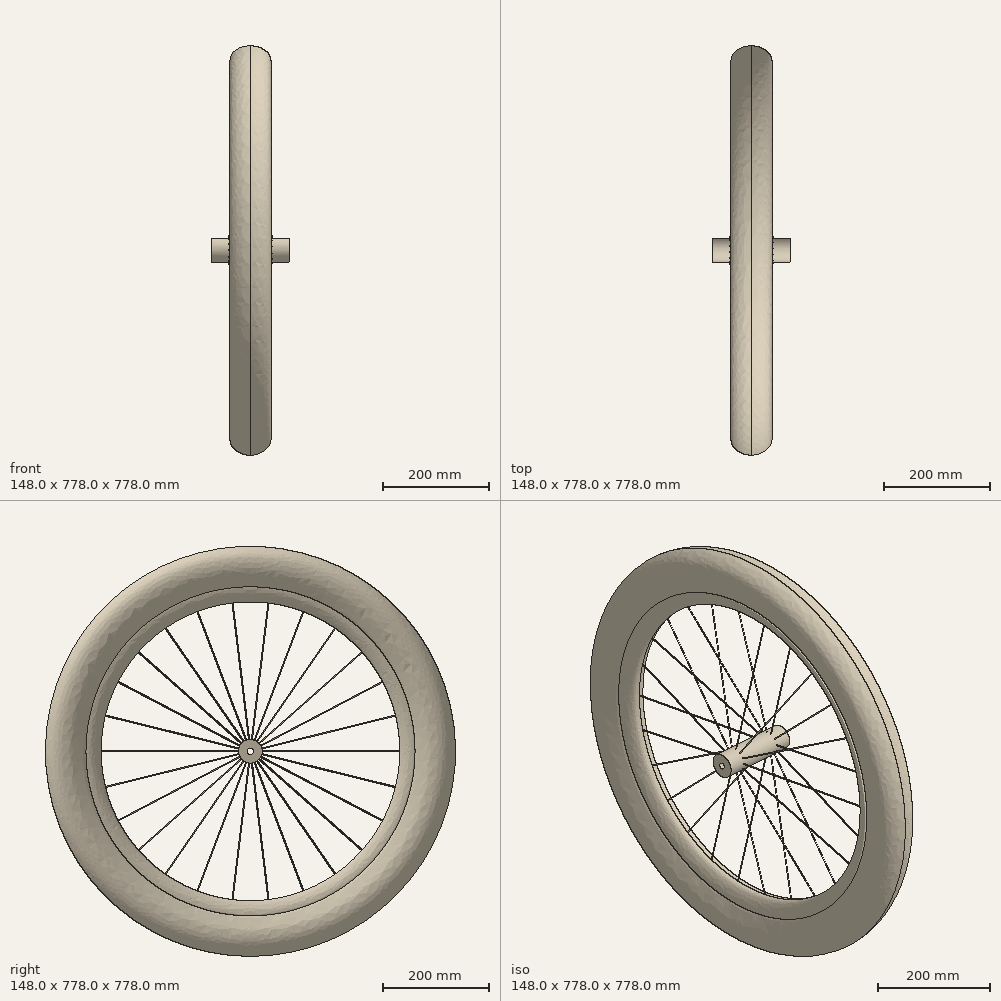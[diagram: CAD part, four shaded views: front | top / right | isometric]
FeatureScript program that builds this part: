
annotation { "Feature Type Name" : "Feature", "Feature Type Description" : "" }
export const myFeature = defineFeature(function(context is Context, id is Id, definition is map)
    precondition{}
    {
        {
            var Q0;
            Q0=qCreatedBy(makeId("Right.planeOp"),FACE);
            var sketch = newSketch(context, id + "F0", { "sketchPlane" : qUnion([Q0])});
            skCircle(sketch, "E0", {"center": v(0, 0) * mm, "radius": 311 * mm});
            skSolve(sketch);
        }
        {
            var Q0;
            Q0=qCreatedBy(makeId("Top.planeOp"),FACE);
            var sketch = newSketch(context, id + "F1", { "sketchPlane" : qUnion([Q0])});
            skFitSpline(sketch, "E1", {"points": [v(20.55, 311.57) * mm, v(21.9, 312.08) * mm, v(23.8, 311.8) * mm, v(24.17, 310.8) * mm, v(23.97, 308.06) * mm, v(22.43, 300.9) * mm, v(12.28, 286.77) * mm, v(0, 283.3) * mm], "startDerivative": vector(8.17, 18.36) * mm, "endDerivative": vector(-81.97, -0.82) * mm});
            skFitSpline(sketch, "E2", {"points": [v(20.55, 311.57) * mm, v(21.24, 310.48) * mm, v(21.34, 310.93) * mm, v(22.97, 310.97) * mm, v(23.15, 310.53) * mm, v(22.53, 305.14) * mm, v(14, 300.56) * mm, v(0, 299.7) * mm], "startDerivative": vector(-17.07, -43.86) * mm, "endDerivative": vector(-49.6, 0.02) * mm});
            skFitSpline(sketch, "E3.MirrorCS", {"points": [v(-20.55, 311.57) * mm, v(-21.9, 312.08) * mm, v(-23.8, 311.8) * mm, v(-24.17, 310.8) * mm, v(-23.97, 308.06) * mm, v(-22.43, 300.9) * mm, v(-12.28, 286.77) * mm, v(0, 283.3) * mm], "startDerivative": vector(-8.17, 18.36) * mm, "endDerivative": vector(81.97, -0.82) * mm});
            skFitSpline(sketch, "E4.MirrorCS", {"points": [v(-20.55, 311.57) * mm, v(-21.24, 310.48) * mm, v(-21.34, 310.93) * mm, v(-22.97, 310.97) * mm, v(-23.15, 310.53) * mm, v(-22.53, 305.14) * mm, v(-14, 300.56) * mm, v(0, 299.7) * mm], "startDerivative": vector(17.07, -43.86) * mm, "endDerivative": vector(49.6, 0.02) * mm});
            skSolve(sketch);
        }
        {
            var Q0;
            Q0=qCreatedBy(makeId("Top.planeOp"),FACE);
            var sketch = newSketch(context, id + "F2", { "sketchPlane" : qUnion([Q0])});
            skFitSpline(sketch, "E5", {"points": [v(22.15, 310.9) * mm, v(21.57, 310.84) * mm, v(21.34, 310.38) * mm, v(20.54, 310.2) * mm, v(20.06, 311.12) * mm, v(20.82, 312.82) * mm, v(24.67, 317.46) * mm, v(31.25, 328.9) * mm, v(37.5, 340.7) * mm, v(38.08, 364.92) * mm, v(25.3, 381.14) * mm, v(0, 389) * mm], "startDerivative": vector(-24.19, 2.88) * mm, "endDerivative": vector(-137.92, 0.5) * mm});
            skFitSpline(sketch, "E6", {"points": [v(22.15, 310.9) * mm, v(22.52, 310.86) * mm, v(22.95, 310.74) * mm, v(23.02, 309.82) * mm, v(22.71, 308.86) * mm, v(21.55, 307.96) * mm, v(19.8, 308.82) * mm, v(19.03, 310.72) * mm, v(20.54, 314.45) * mm, v(26.42, 323.36) * mm, v(32.51, 336.03) * mm, v(36, 347.14) * mm, v(34.97, 365.95) * mm, v(19.79, 381.48) * mm, v(0, 386.48) * mm], "startDerivative": vector(16.59, -2.55) * mm, "endDerivative": vector(-154.7, -0.05) * mm});
            skFitSpline(sketch, "E7.MirrorCS", {"points": [v(-22.15, 310.9) * mm, v(-22.52, 310.86) * mm, v(-22.95, 310.74) * mm, v(-23.02, 309.82) * mm, v(-22.71, 308.86) * mm, v(-21.55, 307.96) * mm, v(-19.8, 308.82) * mm, v(-19.03, 310.72) * mm, v(-20.54, 314.45) * mm, v(-26.42, 323.36) * mm, v(-32.51, 336.03) * mm, v(-36, 347.14) * mm, v(-34.97, 365.95) * mm, v(-19.79, 381.48) * mm, v(0, 386.48) * mm], "startDerivative": vector(-16.59, -2.55) * mm, "endDerivative": vector(154.7, -0.05) * mm});
            skFitSpline(sketch, "E8.MirrorCS", {"points": [v(-22.15, 310.9) * mm, v(-21.57, 310.84) * mm, v(-21.34, 310.38) * mm, v(-20.54, 310.2) * mm, v(-20.06, 311.12) * mm, v(-20.82, 312.82) * mm, v(-24.67, 317.46) * mm, v(-31.25, 328.9) * mm, v(-37.5, 340.7) * mm, v(-38.08, 364.92) * mm, v(-25.3, 381.14) * mm, v(0, 389) * mm], "startDerivative": vector(24.19, 2.88) * mm, "endDerivative": vector(137.92, 0.5) * mm});
            skSolve(sketch);
        }
        {
            var Q0;
            Q0=makeQuery(id+"F1.imprint","IMPRINT",FACE,{"disambiguationData":[TD([[makeQuery(id+"F1.imprint","IMPRINT",EDGE,{"derivedFrom":sQuery(id+"F1.wireOp",EDGE,"E1")}),-1.0]])]});
            var Q1;
            Q1=sQuery(id+"F0.wireOp",EDGE,"E0");
            revolve(context, id + "F3", {"surfaceOperationType" : NewSurfaceOperationType.NEW, "entities" : qUnion([Q0]), "axis" : qUnion([Q1]), "revolveType" : RevolveType.FULL});
        }
        {
            var Q0;
            Q0=makeQuery(id+"F2.imprint","IMPRINT",FACE,{"disambiguationData":[TD([[makeQuery(id+"F2.imprint","IMPRINT",EDGE,{"derivedFrom":sQuery(id+"F2.wireOp",EDGE,"E5")}),1.0]])]});
            var Q1;
            Q1=makeQuery(id+"F3.opRevolve","SWEPT_EDGE",EDGE,{"disambiguationData":[OSD([sQuery(id+"F1.wireOp",EDGE,"E2"),sQuery(id+"F1.wireOp",EDGE,"E4.MirrorCS")])]});
            revolve(context, id + "F4", {"operationType" : NewBodyOperationType.ADD, "surfaceOperationType" : NewSurfaceOperationType.NEW, "entities" : qUnion([Q0]), "axis" : qUnion([Q1]), "revolveType" : RevolveType.FULL});
        }
        {
            var Q0;
            Q0=qCreatedBy(makeId("Right.planeOp"),FACE);
            var sketch = newSketch(context, id + "F5", { "sketchPlane" : qUnion([Q0])});
            skCircle(sketch, "E9", {"center": v(0, 0) * mm, "radius": 6 * mm});
            skCircle(sketch, "E10", {"center": v(0, 0) * mm, "radius": 22.5 * mm});
            skSolve(sketch);
        }
        {
            var Q0;
            Q0=makeQuery(id+"F5.imprint","IMPRINT",FACE,{"disambiguationData":[TD([[makeQuery(id+"F5.imprint","IMPRINT",EDGE,{"derivedFrom":sQuery(id+"F5.wireOp",EDGE,"E9")}),-1.0]])]});
            extrude(context, id + "F6", {"entities" : qUnion([Q0]), "operationType" : NewBodyOperationType.ADD, "depth" : 148 * mm, "offsetDistance" : 25 * mm, "symmetric" : true});
        }
        {
            var Q0;
            Q0=qCreatedBy(makeId("Top.planeOp"),FACE);
            var sketch = newSketch(context, id + "F7", { "sketchPlane" : qUnion([Q0])});
            skLineSegment(sketch, "E11.MirrorCS", {"start": v(0, 283.6) * mm, "end": v(41.7, 20.08) * mm});
            skLineSegment(sketch, "E12.MirrorCS", {"start": v(0, -283.6) * mm, "end": v(-41.7, -20.08) * mm});
            skSolve(sketch);
        }
        {
            var Q0;
            Q0=sQuery(id+"F7.wireOp",EDGE,"E11.MirrorCS");
            var Q1;
            Q1=sQuery(id+"F7.wireOp",VERTEX,"E11.MirrorCS.end");
            cPlane(context, id + "F8", {"entities" : qUnion([Q0, Q1]), "cplaneType" : CPlaneType.LINE_POINT, "offset" : 25 * mm, "width" : 150 * mm, "height" : 150 * mm});
        }
        {
            var Q0;
            Q0=qCreatedBy(id+"F8.planeOp",FACE);
            var sketch = newSketch(context, id + "F9", { "sketchPlane" : qUnion([Q0])});
            skEllipse(sketch, "E13", {"center": v(44.33, 0) * mm, "majorRadius": 1 * mm, "minorRadius": 0.25 * mm, "majorAxis": v(0, 1)});
            skSolve(sketch);
        }
        {
            var Q0;
            Q0=makeQuery(id+"F9.imprint","IMPRINT",FACE,{"disambiguationData":[TD([[makeQuery(id+"F9.imprint","IMPRINT",EDGE,{"derivedFrom":sQuery(id+"F9.wireOp",EDGE,"E13")}),1.0]])]});
            var Q1;
            Q1=sQuery(id+"F7.wireOp",EDGE,"E11.MirrorCS");
            sweep(context, id + "F10", {"profiles" : qUnion([Q0]), "path" : qUnion([Q1])});
        }
        {
            var Q0;
            Q0=qCreatedBy(makeId("Front.planeOp"),FACE);
            var sketch = newSketch(context, id + "F11", { "sketchPlane" : qUnion([Q0])});
            skLineSegment(sketch, "E14", {"start": v(56.16, 0) * mm, "end": v(-56.36, 0) * mm});
            skSolve(sketch);
        }
        {
            var Q0;
            Q0=makeQuery(id+"F10.opSweep","SWEPT_BODY",BODY,{"disambiguationData":[OSD([sQuery(id+"F7.wireOp",EDGE,"E11.MirrorCS"),sQuery(id+"F9.wireOp",EDGE,"E13")])]});
            var Q1;
            Q1=sQuery(id+"F11.wireOp",EDGE,"E14");
            circularPattern(context, id + "F12", {"operationType" : NewBodyOperationType.ADD, "entities" : qUnion([Q0]), "axis" : qUnion([Q1]), "angle" : 360 * degree, "instanceCount" : 13, "equalSpace" : true});
        }
        {
            var Q0;
            Q0=sQuery(id+"F7.wireOp",EDGE,"E12.MirrorCS");
            var Q1;
            Q1=sQuery(id+"F7.wireOp",VERTEX,"E12.MirrorCS.end");
            cPlane(context, id + "F13", {"entities" : qUnion([Q0, Q1]), "cplaneType" : CPlaneType.LINE_POINT, "offset" : 25 * mm, "width" : 150 * mm, "height" : 150 * mm});
        }
        {
            var Q0;
            Q0=qCreatedBy(id+"F13.planeOp",FACE);
            var sketch = newSketch(context, id + "F14", { "sketchPlane" : qUnion([Q0])});
            skEllipse(sketch, "E15", {"center": v(44.33, 0) * mm, "majorRadius": 1 * mm, "minorRadius": 0.25 * mm, "majorAxis": v(0, 1)});
            skSolve(sketch);
        }
        {
            var Q0;
            Q0=makeQuery(id+"F14.imprint","IMPRINT",FACE,{"disambiguationData":[TD([[makeQuery(id+"F14.imprint","IMPRINT",EDGE,{"derivedFrom":sQuery(id+"F14.wireOp",EDGE,"E15")}),1.0]])]});
            var Q1;
            Q1=sQuery(id+"F7.wireOp",EDGE,"E12.MirrorCS");
            sweep(context, id + "F15", {"profiles" : qUnion([Q0]), "path" : qUnion([Q1])});
        }
        {
            var Q0;
            Q0=makeQuery(id+"F15.opSweep","SWEPT_BODY",BODY,{"disambiguationData":[OSD([sQuery(id+"F7.wireOp",EDGE,"E12.MirrorCS"),sQuery(id+"F14.wireOp",EDGE,"E15")])]});
            var Q1;
            Q1=sQuery(id+"F11.wireOp",EDGE,"E14");
            circularPattern(context, id + "F16", {"operationType" : NewBodyOperationType.ADD, "entities" : qUnion([Q0]), "axis" : qUnion([Q1]), "angle" : 360 * degree, "instanceCount" : 13, "equalSpace" : true});
        }
    });
